# Revit family: 3-69 Spirit Pendant
name_source: partatom
category: Lighting Fixtures
revit_build: Autodesk Revit 2018 (Build: 20170223_1515(x64)
units: mm (PartAtom-declared; Revit-internal decimal feet)

## family parameters
Always vertical = Yes
Cut with Voids When Loaded = No
Host = Ceiling
Light Source = Yes
OmniClass Number = 23.80.70.11
OmniClass Title = Luminaries for Internal Lighting
Part Type = Normal
Room Calculation Point = No
Round Connector Dimension = Use Diameter
Shared = No

## types (16) — shared parameters
Color Filter = 16777215
Dimming Lamp Color Temperature Shift = <None>
Lamp = LED
Main Diffuser = Clear Bubble Glass
Manufacturer = Oxygen - Lighting & Fans
Model = 3-69-xxxx-Spirit (Pendant)
Photometric Web File = 3-69-40 Spirit Pendant.ies
References = Ref. 3 = 120 V / Ref. 37 = 277 V
Tilt Angle = 90.00°
URL = www.oxygenlighting.com
Voltage = 120 V
Voltage Input = 120 V or 277 V - 50/60 Hz
Wattage Comments = 7.0 W at 120 V

## per-type parameters (varying)
| type | Metal Finish |
| 3-69-15 / Black - Clear Bubble Glass | 15 - Black |
| 3-69-24 / Satin Nickel - Clear Bubble Glass | 24 - Satin Nickel |
| 3-69-40 / Aged Brass - Clear Bubble Glass | 40 - Aged Brass |
| 3-69-6 / White - Clear Bubble Glass | 40 - Aged Brass |
| 3-69-2715 / Black - Clear Bubble Glass | 15 - Black |
| 3-69-2724 / Satin Nickel - Clear Bubble Glass | 24 - Satin Nickel |
| 3-69-2740 / Aged Brass - Clear Bubble Glass | 40 - Aged Brass |
| 3-69-276 / White - Clear Bubble Glass | 40 - Aged Brass |
| 3-69-3515 / Black - Clear Bubble Glass | 15 - Black |
| 3-69-3524 / Satin Nickel - Clear Bubble Glass | 24 - Satin Nickel |
| 3-69-3540 / Aged Brass - Clear Bubble Glass | 40 - Aged Brass |
| 3-69-356 / White - Clear Bubble Glass | 40 - Aged Brass |
| 3-69-4015 / Black - Clear Bubble Glass | 15 - Black |
| 3-69-4024 / Satin Nickel - Clear Bubble Glass | 24 - Satin Nickel |
| 3-69-406 / White - Clear Bubble Glass | 40 - Aged Brass |
| 3-69-4040 / Aged Brass - Clear Bubble Glass | 40 - Aged Brass |

## geometry (parser evidence)
native form markers: Sweep x2
no freeform markers — native parametric forms only
